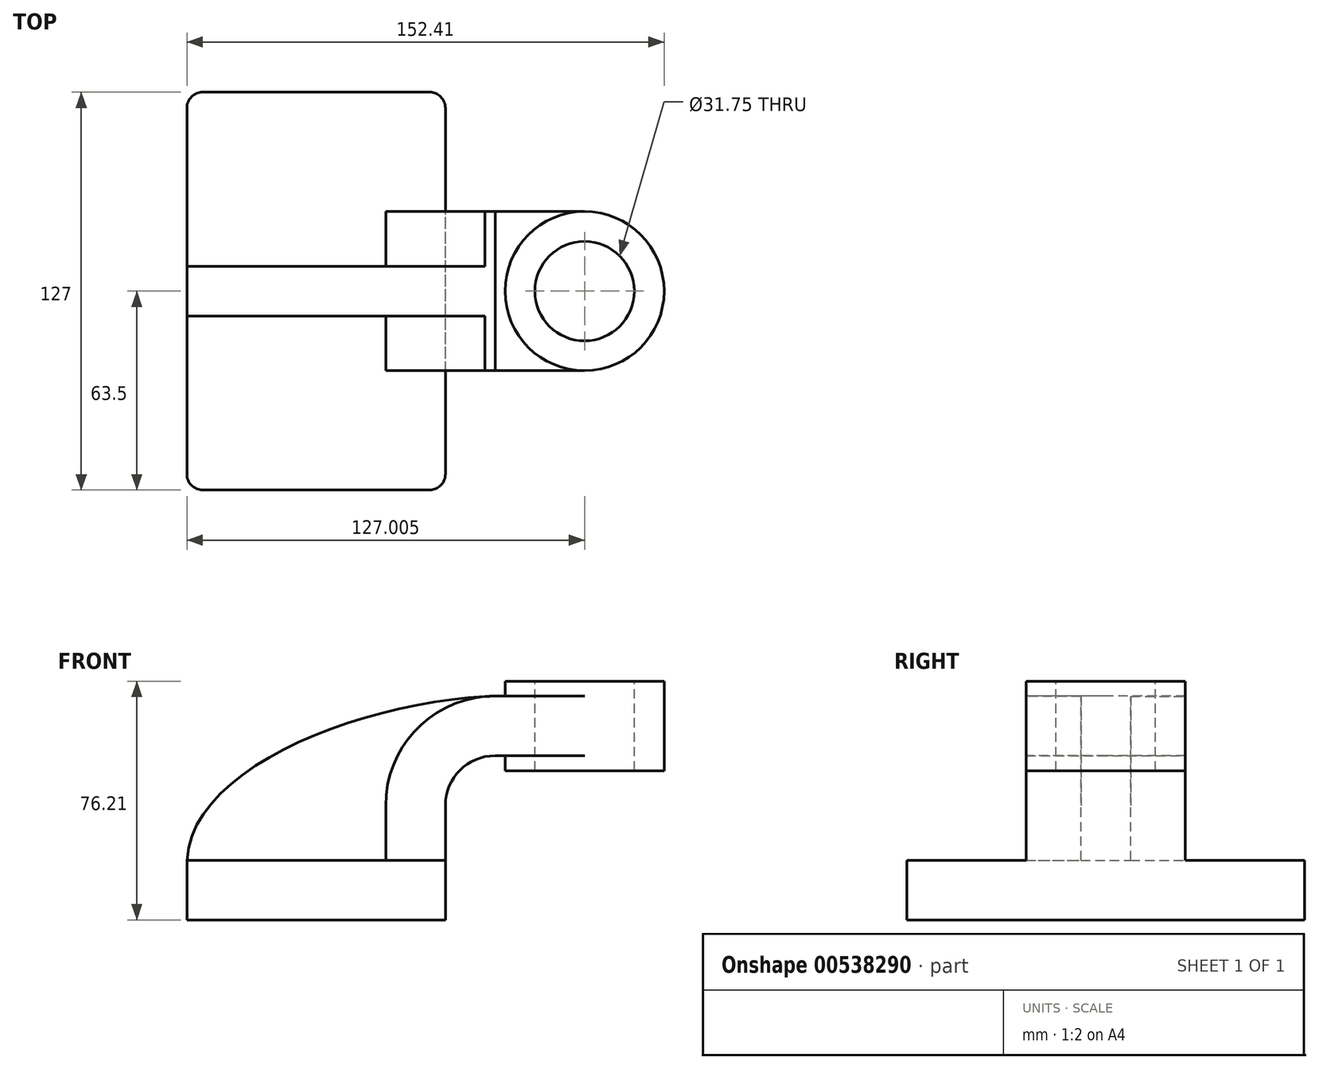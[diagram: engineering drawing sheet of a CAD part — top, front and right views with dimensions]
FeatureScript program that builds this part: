
annotation { "Feature Type Name" : "Feature", "Feature Type Description" : "" }
export const myFeature = defineFeature(function(context is Context, id is Id, definition is map)
    precondition{}
    {
        {
            var Q0;
            Q0=qCreatedBy(makeId("Front.planeOp"),FACE);
            var sketch = newSketch(context, id + "F0", { "sketchPlane" : qUnion([Q0])});
            skLineSegment(sketch, "E0.rect.bottom", {"start": v(-41.28, 9.52) * mm, "end": v(41.28, 9.52) * mm});
            skLineSegment(sketch, "E0.rect.top", {"start": v(-41.28, -9.52) * mm, "end": v(41.28, -9.52) * mm});
            skLineSegment(sketch, "E0.rect.left", {"start": v(-41.28, 9.52) * mm, "end": v(-41.28, -9.52) * mm});
            skLineSegment(sketch, "E0.rect.right", {"start": v(41.28, 9.52) * mm, "end": v(41.28, -9.52) * mm});
            skPoint(sketch, "E0.rect.middle", {"position": v(0, 0) * mm});
            skLineSegment(sketch, "E1", {"start": v(41.28, 9.52) * mm, "end": v(41.28, 27) * mm});
            skArc(sketch, "E2", {"start": v(41.28, 27) * mm, "mid": v(45.92, 38.23) * mm, "end": v(57.15, 42.88) * mm});
            skLineSegment(sketch, "E3", {"start": v(57.15, 42.88) * mm, "end": v(85.72, 42.88) * mm});
            skLineSegment(sketch, "E4.rect.bottom", {"start": v(60.32, 38.1) * mm, "end": v(111.12, 38.1) * mm});
            skLineSegment(sketch, "E4.rect.top", {"start": v(60.32, 66.68) * mm, "end": v(111.12, 66.68) * mm});
            skLineSegment(sketch, "E4.rect.left", {"start": v(60.32, 38.1) * mm, "end": v(60.32, 66.68) * mm});
            skLineSegment(sketch, "E4.rect.right", {"start": v(111.13, 38.1) * mm, "end": v(111.12, 66.68) * mm});
            skPoint(sketch, "E4.rect.middle", {"position": v(85.72, 52.39) * mm});
            skLineSegment(sketch, "E5.0", {"start": v(57.15, 61.93) * mm, "end": v(85.72, 61.93) * mm});
            skArc(sketch, "E5.1", {"start": v(22.23, 27) * mm, "mid": v(32.45, 51.7) * mm, "end": v(57.15, 61.93) * mm});
            skLineSegment(sketch, "E5.2", {"start": v(22.23, 9.52) * mm, "end": v(22.23, 27) * mm});
            skLineSegment(sketch, "E6", {"start": v(85.72, 38.1) * mm, "end": v(85.72, 66.68) * mm});
            skFitSpline(sketch, "E7", {"points": [v(-41.28, 9.53) * mm, v(57.15, 61.93) * mm], "startDerivative": vector(5.2, 92.34) * mm, "endDerivative": vector(120.92, 4.22) * mm});
            skSolve(sketch);
        }
        {
            var Q0;
            Q0=makeQuery(id+"F0.imprint","IMPRINT",FACE,{"disambiguationData":[TD([[makeQuery(id+"F0.imprint","IMPRINT",EDGE,{"derivedFrom":sQuery(id+"F0.wireOp",EDGE,"E0.rect.top")}),1.0]])]});
            extrude(context, id + "F1", {"entities" : qUnion([Q0]), "endBound" : BoundingType.SYMMETRIC, "depth" : 127 * mm});
        }
        {
            var Q0;
            {var subQ9=sQuery(id+"F0.wireOp",EDGE,"E1");Q0=makeQuery(id+"F0.imprint","IMPRINT",FACE,{"disambiguationData":[TD([[makeQuery(id+"F0.imprint","IMPRINT",EDGE,{"derivedFrom":subQ9}),1.0]])]});}
            var Q1;
            {var subQ0=sQuery(id+"F0.wireOp",EDGE,"E6");var subQ1=sQuery(id+"F0.wireOp",EDGE,"E3");var subQ2=makeQuery(id+"F0.imprint","INTERSECT",VERTEX,{"derivedFrom":[subQ1,subQ0]});Q1=makeQuery(id+"F0.imprint","IMPRINT",FACE,{"disambiguationData":[TD([[makeQuery(id+"F0.imprint","IMPRINT",EDGE,{"disambiguationData":[TD([[subQ2,1.0]])],"derivedFrom":subQ1}),1.0]])]});}
            extrude(context, id + "F2", {"entities" : qUnion([Q0, Q1]), "operationType" : NewBodyOperationType.ADD, "endBound" : BoundingType.SYMMETRIC, "depth" : 50.8 * mm});
        }
        {
            var Q0;
            {var subQ3=sQuery(id+"F0.wireOp",EDGE,"E5.2");Q0=makeQuery(id+"F0.imprint","IMPRINT",FACE,{"disambiguationData":[TD([[makeQuery(id+"F0.imprint","IMPRINT",EDGE,{"derivedFrom":subQ3}),1.0]])]});}
            extrude(context, id + "F3", {"entities" : qUnion([Q0]), "operationType" : NewBodyOperationType.ADD, "endBound" : BoundingType.SYMMETRIC, "depth" : 15.88 * mm});
        }
        {
            var Q0;
            {var subQ5=sQuery(id+"F0.wireOp",EDGE,"E4.rect.right");Q0=makeQuery(id+"F0.imprint","IMPRINT",FACE,{"disambiguationData":[TD([[makeQuery(id+"F0.imprint","IMPRINT",EDGE,{"derivedFrom":subQ5}),1.0]])]});}
            var Q1;
            Q1=sQuery(id+"F0.wireOp",EDGE,"E6");
            revolve(context, id + "F4", {"operationType" : NewBodyOperationType.ADD, "entities" : qUnion([Q0]), "axis" : qUnion([Q1]), "revolveType" : RevolveType.FULL});
        }
        {
            var Q0;
            Q0=makeQuery(id+"F1.opExtrude","CAP_EDGE",EDGE,{"disambiguationData":[OSD([sQuery(id+"F0.wireOp",EDGE,"E0.rect.right")])],"isStart":false});
            var Q1;
            Q1=makeQuery(id+"F1.opExtrude","CAP_EDGE",EDGE,{"disambiguationData":[OSD([sQuery(id+"F0.wireOp",EDGE,"E0.rect.left")])],"isStart":false});
            var Q2;
            Q2=makeQuery(id+"F1.opExtrude","CAP_EDGE",EDGE,{"disambiguationData":[OSD([sQuery(id+"F0.wireOp",EDGE,"E0.rect.right")])],"isStart":true});
            var Q3;
            Q3=makeQuery(id+"F1.opExtrude","CAP_EDGE",EDGE,{"disambiguationData":[OSD([sQuery(id+"F0.wireOp",EDGE,"E0.rect.left")])],"isStart":true});
            fillet(context, id + "F5", {"entities" : qUnion([Q0, Q1, Q2, Q3]), "radius" : 5.08 * mm, "tangentPropagation" : true, "allowEdgeOverflow" : false});
        }
        {
            var Q0;
            Q0=makeQuery(id+"F4.opRevolve","SWEPT_FACE",FACE,{"disambiguationData":[OSD([sQuery(id+"F0.wireOp",EDGE,"E4.rect.top")])]});
            var sketch = newSketch(context, id + "F6", { "sketchPlane" : qUnion([Q0])});
            skCircle(sketch, "E8", {"center": v(85.72, 0) * mm, "radius": 15.88 * mm});
            skSolve(sketch);
        }
        {
            var Q0;
            Q0 = qSketchRegion(id + "F6", true);
            extrude(context, id + "F7", {"entities" : qUnion([Q0]), "operationType" : NewBodyOperationType.REMOVE, "oppositeDirection" : true, "depth" : 46.74 * mm, "offsetDistance" : 25.4 * mm});
        }
    });
